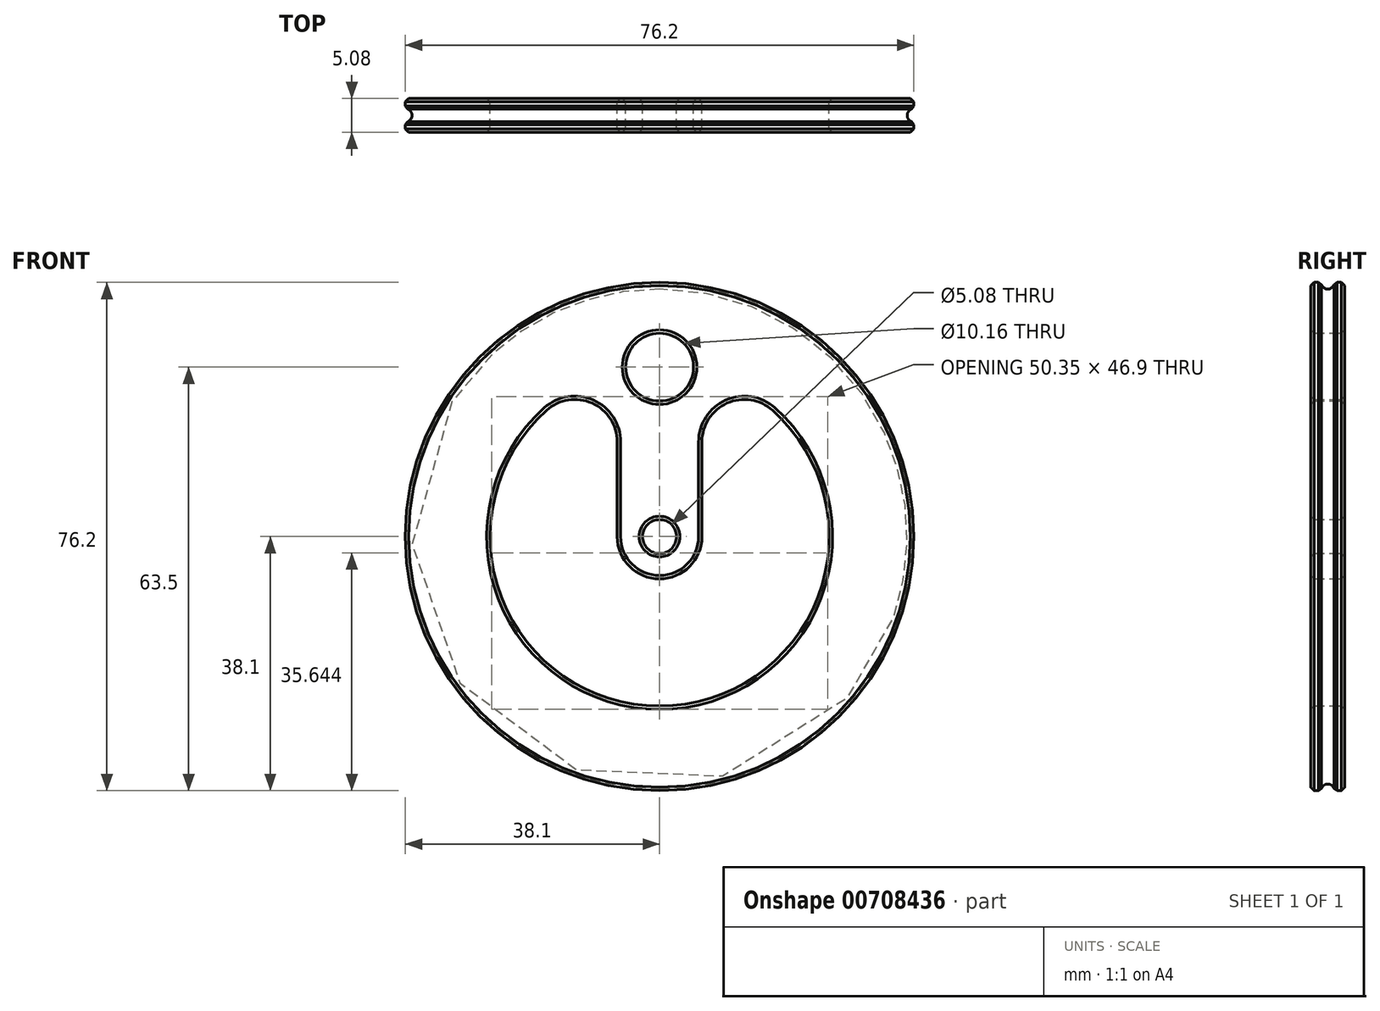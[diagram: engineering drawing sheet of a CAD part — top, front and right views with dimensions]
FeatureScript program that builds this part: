
annotation { "Feature Type Name" : "Feature", "Feature Type Description" : "" }
export const myFeature = defineFeature(function(context is Context, id is Id, definition is map)
    precondition{}
    {
        {
            var Q0;
            Q0=qCreatedBy(makeId("Front.planeOp"),FACE);
            var sketch = newSketch(context, id + "F0", { "sketchPlane" : qUnion([Q0])});
            skCircle(sketch, "E0", {"center": v(0, 0) * mm, "radius": 38.1 * mm});
            skArc(sketch, "E1", {"start": v(-16.93, 18.93) * mm, "mid": v(0, -25.4) * mm, "end": v(16.93, 18.93) * mm});
            skLineSegment(sketch, "E2.top", {"start": v(0, -6.35) * mm, "end": v(0, -6.35) * mm});
            skLineSegment(sketch, "E2.left", {"start": v(-6.35, 14.2) * mm, "end": v(-6.35, 0) * mm});
            skLineSegment(sketch, "E2.right", {"start": v(6.35, 14.2) * mm, "end": v(6.35, 0) * mm});
            skPoint(sketch, "E3.visualSharp", {"position": v(-6.35, -6.35) * mm});
            skArc(sketch, "E3.filletArc", {"start": v(-6.35, 0) * mm, "mid": v(-4.5, -4.5) * mm, "end": v(0, -6.35) * mm});
            skPoint(sketch, "E4.visualSharp", {"position": v(6.35, -6.35) * mm});
            skArc(sketch, "E4.filletArc", {"start": v(0, -6.35) * mm, "mid": v(4.5, -4.5) * mm, "end": v(6.35, 0) * mm});
            skPoint(sketch, "E5.visualSharp", {"position": v(6.35, 24.6) * mm});
            skArc(sketch, "E5.filletArc", {"start": v(16.93, 18.93) * mm, "mid": v(10.1, 20) * mm, "end": v(6.35, 14.2) * mm});
            skPoint(sketch, "E6.visualSharp", {"position": v(-6.35, 24.6) * mm});
            skArc(sketch, "E6.filletArc", {"start": v(-6.35, 14.2) * mm, "mid": v(-10.1, 20) * mm, "end": v(-16.93, 18.93) * mm});
            skCircle(sketch, "E7", {"center": v(0, 0) * mm, "radius": 2.54 * mm});
            skCircle(sketch, "E8", {"center": v(0, 25.4) * mm, "radius": 5.08 * mm});
            skSolve(sketch);
        }
        {
            var Q0;
            Q0=makeQuery(id+"F0.imprint","IMPRINT",FACE,{"disambiguationData":[TD([[makeQuery(id+"F0.imprint","IMPRINT",EDGE,{"derivedFrom":sQuery(id+"F0.wireOp",EDGE,"E0")}),1.0]])]});
            extrude(context, id + "F1", {"entities" : qUnion([Q0]), "depth" : 5.08 * mm, "offsetDistance" : 25.4 * mm});
        }
        {
            var Q0;
            Q0=qCreatedBy(makeId("Right.planeOp"),FACE);
            var sketch = newSketch(context, id + "F2", { "sketchPlane" : qUnion([Q0])});
            skCircle(sketch, "E9", {"center": v(-2.54, 38.1) * mm, "radius": 1 * mm});
            skLineSegment(sketch, "E10", {"start": v(-0.5, -38.1) * mm, "end": v(-4.57, -38.1) * mm});
            skLineSegment(sketch, "E11", {"start": v(-4.57, 38.1) * mm, "end": v(-0.5, 38.1) * mm});
            skSolve(sketch);
        }
        {
            var Q0;
            {var subQ0=sQuery(id+"F2.wireOp",EDGE,"E11");var subQ1=sQuery(id+"F2.wireOp",EDGE,"E9");var subQ2=makeQuery(id+"F2.imprint","INTERSECT",VERTEX,{"disambiguationData":[OD(0.0)],"derivedFrom":[subQ1,subQ0]});Q0=makeQuery(id+"F2.imprint","IMPRINT",FACE,{"disambiguationData":[TD([[makeQuery(id+"F2.imprint","IMPRINT",EDGE,{"disambiguationData":[TD([[subQ2,1.0]])],"derivedFrom":subQ1}),1.0]])]});}
            var Q1;
            {var subQ0=sQuery(id+"F2.wireOp",EDGE,"E11");var subQ1=sQuery(id+"F2.wireOp",EDGE,"E9");var subQ2=makeQuery(id+"F2.imprint","INTERSECT",VERTEX,{"disambiguationData":[OD(0.0)],"derivedFrom":[subQ1,subQ0]});Q1=makeQuery(id+"F2.imprint","IMPRINT",FACE,{"disambiguationData":[TD([[makeQuery(id+"F2.imprint","IMPRINT",EDGE,{"disambiguationData":[TD([[subQ2,-1.0]])],"derivedFrom":subQ1}),1.0]])]});}
            var Q2;
            Q2=sQuery(id+"F2.wireOp",EDGE,"E9");
            var Q3;
            Q3=makeQuery(id+"F1.opExtrude","CAP_EDGE",EDGE,{"disambiguationData":[OSD([sQuery(id+"F0.wireOp",EDGE,"E7")])],"isStart":true});
            revolve(context, id + "F3", {"surfaceOperationType" : NewSurfaceOperationType.NEW, "entities" : qUnion([Q0, Q1]), "surfaceEntities" : qUnion([Q2]), "axis" : qUnion([Q3]), "revolveType" : RevolveType.FULL});
        }
        {
            var Q0;
            Q0=makeQuery(id+"F3.opRevolve","SWEPT_BODY",BODY,{"disambiguationData":[OSD([sQuery(id+"F2.wireOp",EDGE,"E9")])]});
            var Q1;
            Q1=makeQuery(id+"F1.opExtrude","SWEPT_BODY",BODY,{"disambiguationData":[OSD([sQuery(id+"F0.wireOp",EDGE,"E0"),sQuery(id+"F0.wireOp",EDGE,"E1"),sQuery(id+"F0.wireOp",EDGE,"E2.left"),sQuery(id+"F0.wireOp",EDGE,"E2.right"),sQuery(id+"F0.wireOp",EDGE,"E3.filletArc"),sQuery(id+"F0.wireOp",EDGE,"E4.filletArc"),sQuery(id+"F0.wireOp",EDGE,"E5.filletArc"),sQuery(id+"F0.wireOp",EDGE,"E6.filletArc"),sQuery(id+"F0.wireOp",EDGE,"E7"),sQuery(id+"F0.wireOp",EDGE,"E8")])]});
            booleanBodies(context, id + "F4", {"operationType" : BooleanOperationType.SUBTRACTION, "tools" : qUnion([Q0]), "targets" : qUnion([Q1])});
        }
        {
            var Q0;
            Q0=makeQuery(id+"F1.opExtrude","CAP_FACE",FACE,{"disambiguationData":[OSD([sQuery(id+"F0.wireOp",EDGE,"E0"),sQuery(id+"F0.wireOp",EDGE,"E1"),sQuery(id+"F0.wireOp",EDGE,"E2.left"),sQuery(id+"F0.wireOp",EDGE,"E2.right"),sQuery(id+"F0.wireOp",EDGE,"E3.filletArc"),sQuery(id+"F0.wireOp",EDGE,"E4.filletArc"),sQuery(id+"F0.wireOp",EDGE,"E5.filletArc"),sQuery(id+"F0.wireOp",EDGE,"E6.filletArc")])],"isStart":false});
            var Q1;
            Q1=makeQuery(id+"F1.opExtrude","CAP_FACE",FACE,{"disambiguationData":[OSD([sQuery(id+"F0.wireOp",EDGE,"E0"),sQuery(id+"F0.wireOp",EDGE,"E1"),sQuery(id+"F0.wireOp",EDGE,"E2.left"),sQuery(id+"F0.wireOp",EDGE,"E2.right"),sQuery(id+"F0.wireOp",EDGE,"E3.filletArc"),sQuery(id+"F0.wireOp",EDGE,"E4.filletArc"),sQuery(id+"F0.wireOp",EDGE,"E5.filletArc"),sQuery(id+"F0.wireOp",EDGE,"E6.filletArc")])],"isStart":true});
            var Q2;
            Q2=makeQuery(id+"F4.opBoolean","INTERSECT",EDGE,{"disambiguationData":[OD(1.0)],"derivedFrom":[makeQuery(id+"F1.opExtrude","SWEPT_FACE",FACE,{"disambiguationData":[OSD([sQuery(id+"F0.wireOp",EDGE,"E0")])]}),makeQuery(id+"F3.opRevolve","SWEPT_FACE",FACE,{"disambiguationData":[OSD([sQuery(id+"F2.wireOp",EDGE,"E9")])]})]});
            var Q3;
            Q3=makeQuery(id+"F4.opBoolean","INTERSECT",EDGE,{"disambiguationData":[OD(0.0)],"derivedFrom":[makeQuery(id+"F1.opExtrude","SWEPT_FACE",FACE,{"disambiguationData":[OSD([sQuery(id+"F0.wireOp",EDGE,"E0")])]}),makeQuery(id+"F3.opRevolve","SWEPT_FACE",FACE,{"disambiguationData":[OSD([sQuery(id+"F2.wireOp",EDGE,"E9")])]})]});
            chamfer(context, id + "F5", {"entities" : qUnion([Q0, Q1, Q2, Q3]), "width" : 0.5 * mm, "tangentPropagation" : true});
        }
    });
